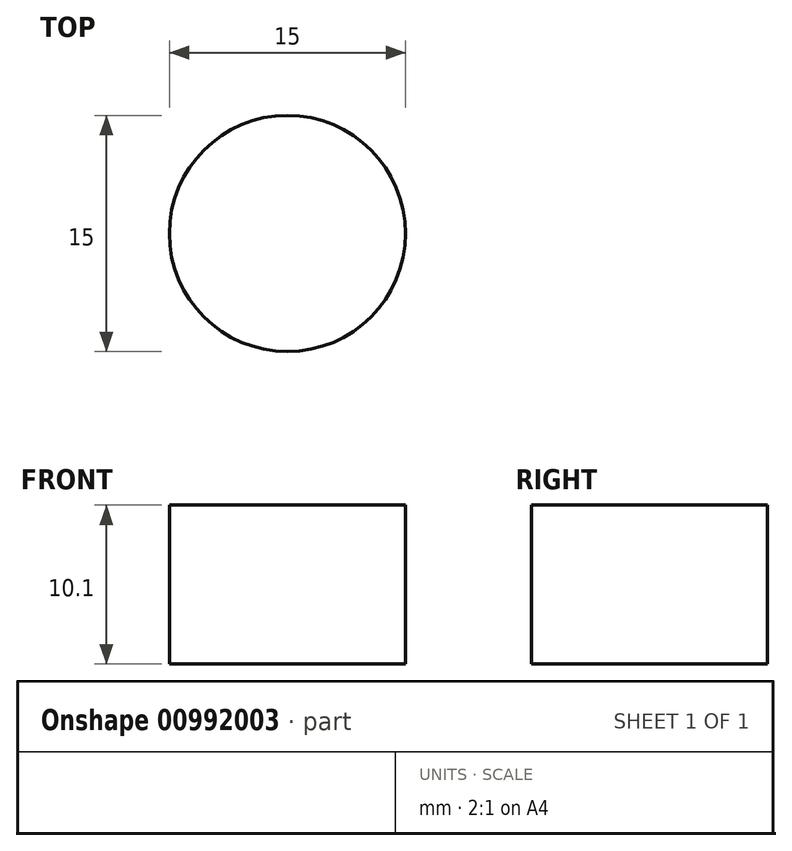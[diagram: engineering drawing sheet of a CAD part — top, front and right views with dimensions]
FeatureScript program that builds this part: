
annotation { "Feature Type Name" : "Feature", "Feature Type Description" : "" }
export const myFeature = defineFeature(function(context is Context, id is Id, definition is map)
    precondition{}
    {
        {
            var Q0;
            Q0=qCreatedBy(makeId("Top.planeOp"),FACE);
            var sketch = newSketch(context, id + "F0", { "sketchPlane" : qUnion([Q0])});
            skCircle(sketch, "E0", {"center": v(0, 0) * mm, "radius": 12.5 * mm});
            skCircle(sketch, "E1", {"center": v(0, 0) * mm, "radius": 7.5 * mm});
            skSolve(sketch);
        }
        {
            var Q0;
            Q0=makeQuery(id+"F0.imprint","IMPRINT",FACE,{"disambiguationData":[TD([[makeQuery(id+"F0.imprint","IMPRINT",EDGE,{"derivedFrom":sQuery(id+"F0.wireOp",EDGE,"E1")}),1.0]])]});
            extrude(context, id + "F1", {"entities" : qUnion([Q0]), "depth" : 10.1 * mm, "offsetDistance" : 25 * mm});
        }
    });
